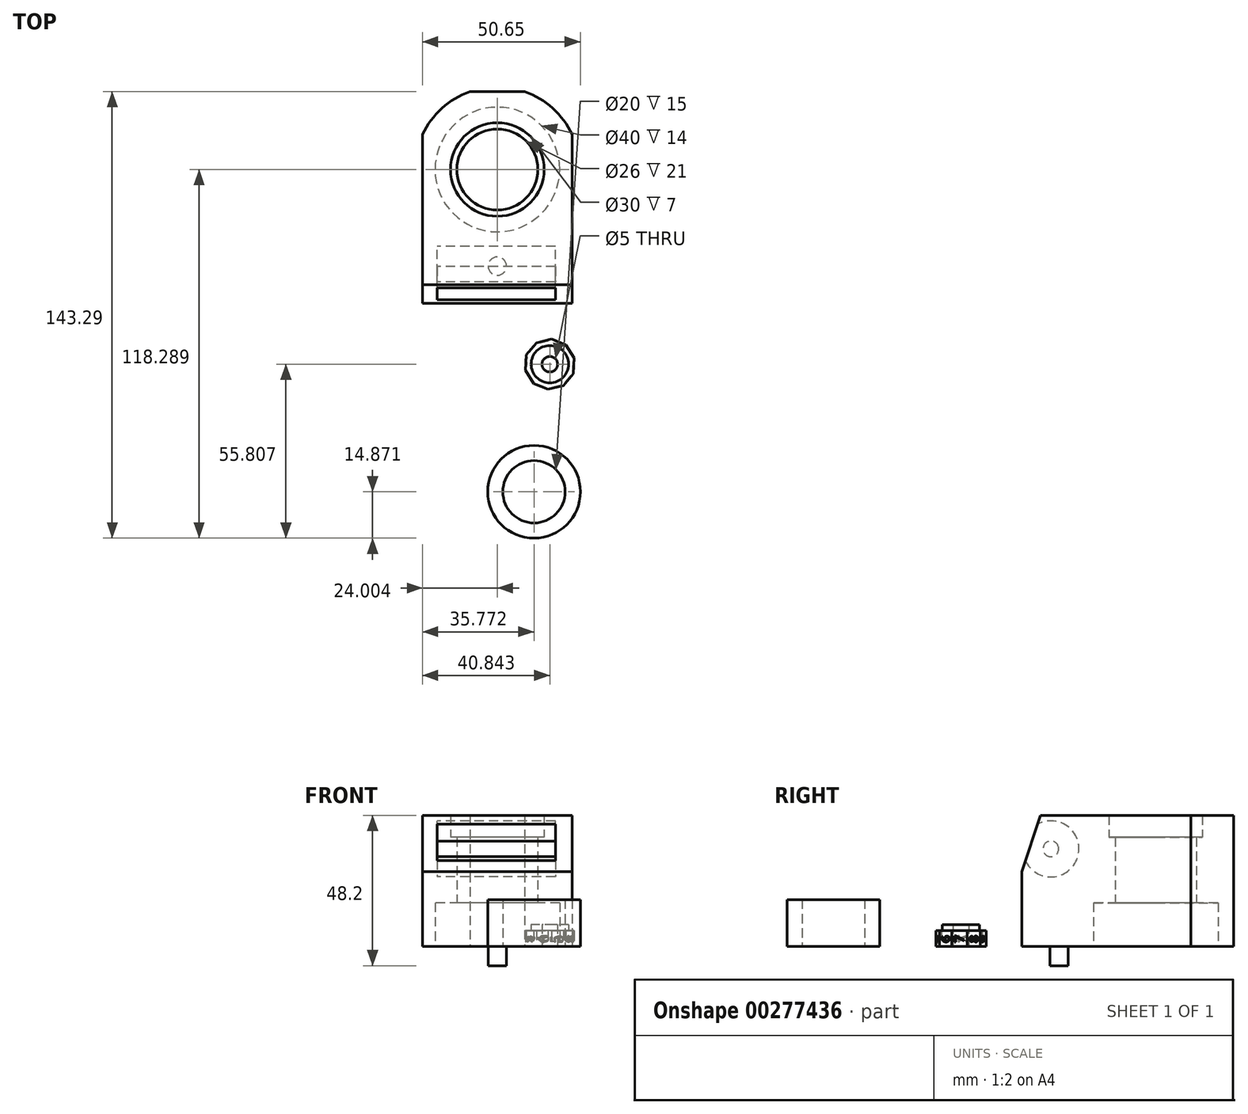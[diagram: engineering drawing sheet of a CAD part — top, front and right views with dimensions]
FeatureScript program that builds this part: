
annotation { "Feature Type Name" : "Feature", "Feature Type Description" : "" }
export const myFeature = defineFeature(function(context is Context, id is Id, definition is map)
    precondition{}
    {
        {
            var Q0;
            Q0=qCreatedBy(makeId("Top.planeOp"),FACE);
            var sketch = newSketch(context, id + "F0", { "sketchPlane" : qUnion([Q0])});
            skCircle(sketch, "E0.cCircle", {"center": v(-31.33, 0.84) * mm, "radius": 7.7 * mm, "construction": true});
            skLineSegment(sketch, "E0.0", {"start": v(-23.82, -2.17) * mm, "end": v(-27.02, -6) * mm});
            skLineSegment(sketch, "E0.1", {"start": v(-27.02, -6) * mm, "end": v(-31.86, -7.23) * mm});
            skLineSegment(sketch, "E0.2", {"start": v(-31.86, -7.23) * mm, "end": v(-36.5, -5.38) * mm});
            skLineSegment(sketch, "E0.3", {"start": v(-36.5, -5.38) * mm, "end": v(-39.17, -1.15) * mm});
            skLineSegment(sketch, "E0.4", {"start": v(-39.17, -1.15) * mm, "end": v(-38.84, 3.84) * mm});
            skLineSegment(sketch, "E0.5", {"start": v(-38.84, 3.84) * mm, "end": v(-35.64, 7.68) * mm});
            skLineSegment(sketch, "E0.6", {"start": v(-35.64, 7.68) * mm, "end": v(-30.8, 8.9) * mm});
            skLineSegment(sketch, "E0.7", {"start": v(-30.8, 8.9) * mm, "end": v(-26.15, 7.05) * mm});
            skLineSegment(sketch, "E0.8", {"start": v(-26.15, 7.05) * mm, "end": v(-23.48, 2.82) * mm});
            skLineSegment(sketch, "E0.9", {"start": v(-23.48, 2.82) * mm, "end": v(-23.82, -2.17) * mm});
            skPoint(sketch, "E0.0.midPoint", {"position": v(-25.42, -4.09) * mm});
            skCircle(sketch, "E1", {"center": v(-31.33, 0.84) * mm, "radius": 2.5 * mm});
            skSolve(sketch);
        }
        {
            var Q0;
            Q0=makeQuery(id+"F0.imprint","IMPRINT",FACE,{"disambiguationData":[TD([[makeQuery(id+"F0.imprint","IMPRINT",EDGE,{"derivedFrom":sQuery(id+"F0.wireOp",EDGE,"E0.0")}),-1.0]])]});
            extrude(context, id + "F1", {"entities" : qUnion([Q0]), "depth" : 5 * mm});
        }
        {
            var Q0;
            Q0=makeQuery(id+"F1.opExtrude","CAP_FACE",FACE,{"disambiguationData":[OSD([sQuery(id+"F0.wireOp",EDGE,"E0.0"),sQuery(id+"F0.wireOp",EDGE,"E0.1"),sQuery(id+"F0.wireOp",EDGE,"E0.2"),sQuery(id+"F0.wireOp",EDGE,"E0.3"),sQuery(id+"F0.wireOp",EDGE,"E0.4"),sQuery(id+"F0.wireOp",EDGE,"E0.5"),sQuery(id+"F0.wireOp",EDGE,"E0.6"),sQuery(id+"F0.wireOp",EDGE,"E0.7"),sQuery(id+"F0.wireOp",EDGE,"E0.8"),sQuery(id+"F0.wireOp",EDGE,"E0.9"),sQuery(id+"F0.wireOp",EDGE,"E1")])],"isStart":false});
            var sketch = newSketch(context, id + "F2", { "sketchPlane" : qUnion([Q0])});
            skCircle(sketch, "E2", {"center": v(-31.33, 0.84) * mm, "radius": 6 * mm});
            skSolve(sketch);
        }
        {
            var Q0;
            Q0=makeQuery(id+"F2.imprint","IMPRINT",FACE,{"disambiguationData":[TD([[makeQuery(id+"F2.imprint","IMPRINT",EDGE,{"derivedFrom":sQuery(id+"F2.wireOp",EDGE,"E2")}),1.0]])]});
            extrude(context, id + "F3", {"entities" : qUnion([Q0]), "operationType" : NewBodyOperationType.ADD, "depth" : 2 * mm});
        }
        {
            var Q0;
            Q0=makeQuery(id+"F1.opExtrude","SWEPT_FACE",FACE,{"disambiguationData":[OSD([sQuery(id+"F0.wireOp",EDGE,"E0.6")])]});
            var sketch = newSketch(context, id + "F4", { "sketchPlane" : qUnion([Q0])});
            skText(sketch, "E3", { "text": "0", "fontName": "OpenSans-Regular.ttf"});
            const initialGuessF4  = {"E3": [0.02861, 0.00365, 0, -1, 0.003]};
            skSetInitialGuess(sketch, initialGuessF4);
            skSolve(sketch);
        }
        {
            var Q0;
            Q0 = qSketchRegion(id + "F4", true);
            extrude(context, id + "F5", {"entities" : qUnion([Q0]), "operationType" : NewBodyOperationType.REMOVE, "oppositeDirection" : true, "depth" : 0.2 * mm});
        }
        {
            var Q0;
            Q0=makeQuery(id+"F1.opExtrude","SWEPT_FACE",FACE,{"disambiguationData":[OSD([sQuery(id+"F0.wireOp",EDGE,"E0.5")])]});
            var sketch = newSketch(context, id + "F6", { "sketchPlane" : qUnion([Q0])});
            skText(sketch, "E4", { "text": "1", "fontName": "OpenSans-Regular.ttf"});
            const initialGuessF6  = {"E4": [0.0208, 0.00138, 0, 1, 0.003]};
            skSetInitialGuess(sketch, initialGuessF6);
            skSolve(sketch);
        }
        {
            var Q0;
            Q0 = qSketchRegion(id + "F6", true);
            extrude(context, id + "F7", {"entities" : qUnion([Q0]), "operationType" : NewBodyOperationType.REMOVE, "oppositeDirection" : true, "depth" : 0.2 * mm});
        }
        {
            var Q0;
            Q0=makeQuery(id+"F1.opExtrude","SWEPT_FACE",FACE,{"disambiguationData":[OSD([sQuery(id+"F0.wireOp",EDGE,"E0.4")])]});
            var sketch = newSketch(context, id + "F8", { "sketchPlane" : qUnion([Q0])});
            skText(sketch, "E5", { "text": "2", "fontName": "OpenSans-Regular.ttf"});
            const initialGuessF8  = {"E5": [0.00264, 0.00125, 0, 1, 0.003]};
            skSetInitialGuess(sketch, initialGuessF8);
            skSolve(sketch);
        }
        {
            var Q0;
            Q0 = qSketchRegion(id + "F8", true);
            extrude(context, id + "F9", {"entities" : qUnion([Q0]), "operationType" : NewBodyOperationType.REMOVE, "oppositeDirection" : true, "depth" : 0.2 * mm});
        }
        {
            var Q0;
            Q0=makeQuery(id+"F1.opExtrude","SWEPT_FACE",FACE,{"disambiguationData":[OSD([sQuery(id+"F0.wireOp",EDGE,"E0.3")])]});
            var sketch = newSketch(context, id + "F10", { "sketchPlane" : qUnion([Q0])});
            skText(sketch, "E6", { "text": "3", "fontName": "OpenSans-Regular.ttf"});
            const initialGuessF10  = {"E6": [-0.01597, 0.00116, 0, 1, 0.003]};
            skSetInitialGuess(sketch, initialGuessF10);
            skSolve(sketch);
        }
        {
            var Q0;
            Q0 = qSketchRegion(id + "F10", true);
            extrude(context, id + "F11", {"entities" : qUnion([Q0]), "operationType" : NewBodyOperationType.REMOVE, "oppositeDirection" : true, "depth" : 0.2 * mm});
        }
        {
            var Q0;
            Q0=makeQuery(id+"F1.opExtrude","SWEPT_FACE",FACE,{"disambiguationData":[OSD([sQuery(id+"F0.wireOp",EDGE,"E0.2")])]});
            var sketch = newSketch(context, id + "F12", { "sketchPlane" : qUnion([Q0])});
            skText(sketch, "E7", { "text": "4", "fontName": "OpenSans-Regular.ttf"});
            const initialGuessF12  = {"E7": [-0.02786, 0.00106, 0, 1, 0.003]};
            skSetInitialGuess(sketch, initialGuessF12);
            skSolve(sketch);
        }
        {
            var Q0;
            Q0 = qSketchRegion(id + "F12", true);
            extrude(context, id + "F13", {"entities" : qUnion([Q0]), "operationType" : NewBodyOperationType.REMOVE, "oppositeDirection" : true, "depth" : 0.2 * mm});
        }
        {
            var Q0;
            Q0=makeQuery(id+"F1.opExtrude","SWEPT_FACE",FACE,{"disambiguationData":[OSD([sQuery(id+"F0.wireOp",EDGE,"E0.1")])]});
            var sketch = newSketch(context, id + "F14", { "sketchPlane" : qUnion([Q0])});
            skText(sketch, "E8", { "text": "5", "fontName": "OpenSans-Regular.ttf"});
            const initialGuessF14  = {"E8": [-0.0288, 0.00105, 0, 1, 0.003]};
            skSetInitialGuess(sketch, initialGuessF14);
            skSolve(sketch);
        }
        {
            var Q0;
            Q0 = qSketchRegion(id + "F14", true);
            extrude(context, id + "F15", {"entities" : qUnion([Q0]), "operationType" : NewBodyOperationType.REMOVE, "oppositeDirection" : true, "depth" : 0.2 * mm});
        }
        {
            var Q0;
            Q0=makeQuery(id+"F1.opExtrude","SWEPT_FACE",FACE,{"disambiguationData":[OSD([sQuery(id+"F0.wireOp",EDGE,"E0.0")])]});
            var sketch = newSketch(context, id + "F16", { "sketchPlane" : qUnion([Q0])});
            skText(sketch, "E9", { "text": "6", "fontName": "OpenSans-Regular.ttf"});
            const initialGuessF16  = {"E9": [-0.0179, 0.00116, 0, 1, 0.003]};
            skSetInitialGuess(sketch, initialGuessF16);
            skSolve(sketch);
        }
        {
            var Q0;
            Q0 = qSketchRegion(id + "F16", true);
            extrude(context, id + "F17", {"entities" : qUnion([Q0]), "operationType" : NewBodyOperationType.REMOVE, "oppositeDirection" : true, "depth" : 0.2 * mm});
        }
        {
            var Q0;
            Q0=makeQuery(id+"F1.opExtrude","SWEPT_FACE",FACE,{"disambiguationData":[OSD([sQuery(id+"F0.wireOp",EDGE,"E0.9")])]});
            var sketch = newSketch(context, id + "F18", { "sketchPlane" : qUnion([Q0])});
            skText(sketch, "E10", { "text": "7", "fontName": "OpenSans-Regular.ttf"});
            const initialGuessF18  = {"E10": [0.00025, 0.00121, 0, 1, 0.003]};
            skSetInitialGuess(sketch, initialGuessF18);
            skSolve(sketch);
        }
        {
            var Q0;
            Q0 = qSketchRegion(id + "F18", true);
            extrude(context, id + "F19", {"entities" : qUnion([Q0]), "operationType" : NewBodyOperationType.REMOVE, "oppositeDirection" : true, "depth" : 0.2 * mm});
        }
        {
            var Q0;
            Q0=makeQuery(id+"F1.opExtrude","SWEPT_FACE",FACE,{"disambiguationData":[OSD([sQuery(id+"F0.wireOp",EDGE,"E0.8")])]});
            var sketch = newSketch(context, id + "F20", { "sketchPlane" : qUnion([Q0])});
            skText(sketch, "E11", { "text": "8", "fontName": "OpenSans-Regular.ttf"});
            const initialGuessF20  = {"E11": [0.01895, 0.00118, 0, 1, 0.003]};
            skSetInitialGuess(sketch, initialGuessF20);
            skSolve(sketch);
        }
        {
            var Q0;
            Q0 = qSketchRegion(id + "F20", true);
            extrude(context, id + "F21", {"entities" : qUnion([Q0]), "operationType" : NewBodyOperationType.REMOVE, "oppositeDirection" : true, "depth" : 0.2 * mm});
        }
        {
            var Q0;
            Q0=makeQuery(id+"F1.opExtrude","SWEPT_FACE",FACE,{"disambiguationData":[OSD([sQuery(id+"F0.wireOp",EDGE,"E0.7")])]});
            var sketch = newSketch(context, id + "F22", { "sketchPlane" : qUnion([Q0])});
            skText(sketch, "E12", { "text": "9", "fontName": "OpenSans-Regular.ttf"});
            const initialGuessF22  = {"E12": [0.03078, 0.0011, 0, 1, 0.003]};
            skSetInitialGuess(sketch, initialGuessF22);
            skSolve(sketch);
        }
        {
            var Q0;
            Q0 = qSketchRegion(id + "F22", true);
            extrude(context, id + "F23", {"entities" : qUnion([Q0]), "operationType" : NewBodyOperationType.REMOVE, "oppositeDirection" : true, "depth" : 0.2 * mm});
        }
        {
            var Q0;
            Q0=qCreatedBy(makeId("Top.planeOp"),FACE);
            var sketch = newSketch(context, id + "F24", { "sketchPlane" : qUnion([Q0])});
            skLineSegment(sketch, "E13.bottom", {"start": v(-56.96, 88.32) * mm, "end": v(-39.38, 88.32) * mm});
            skLineSegment(sketch, "E13.top", {"start": v(-72.17, 20.32) * mm, "end": v(-24.17, 20.32) * mm});
            skLineSegment(sketch, "E13.left", {"start": v(-72.17, 74.55) * mm, "end": v(-72.17, 20.32) * mm});
            skLineSegment(sketch, "E13.right", {"start": v(-24.17, 74.55) * mm, "end": v(-24.17, 20.32) * mm});
            skArc(sketch, "E14", {"start": v(-56.96, 88.32) * mm, "mid": v(-65.95, 82.97) * mm, "end": v(-72.17, 74.55) * mm});
            skPoint(sketch, "E14.centerSnap0", {"position": v(-48.17, 88.32) * mm});
            skPoint(sketch, "E15.orphan", {"position": v(-72.17, 88.32) * mm});
            skArc(sketch, "E16.trimOffspring", {"start": v(-24.17, 74.55) * mm, "mid": v(-30.39, 82.97) * mm, "end": v(-39.38, 88.32) * mm});
            skPoint(sketch, "E17.orphan", {"position": v(-24.17, 88.32) * mm});
            skCircle(sketch, "E18", {"center": v(-48.17, 63.32) * mm, "radius": 20 * mm});
            skSolve(sketch);
        }
        {
            var Q0;
            Q0=makeQuery(id+"F24.imprint","IMPRINT",FACE,{"disambiguationData":[TD([[makeQuery(id+"F24.imprint","IMPRINT",EDGE,{"derivedFrom":sQuery(id+"F24.wireOp",EDGE,"E13.bottom")}),-1.0]])]});
            extrude(context, id + "F25", {"entities" : qUnion([Q0]), "depth" : 14 * mm});
        }
        {
            var Q0;
            Q0=makeQuery(id+"F25.opExtrude","CAP_FACE",FACE,{"disambiguationData":[OSD([sQuery(id+"F24.wireOp",EDGE,"E13.bottom"),sQuery(id+"F24.wireOp",EDGE,"E13.top"),sQuery(id+"F24.wireOp",EDGE,"E13.left"),sQuery(id+"F24.wireOp",EDGE,"E13.right"),sQuery(id+"F24.wireOp",EDGE,"E14"),sQuery(id+"F24.wireOp",EDGE,"E16.trimOffspring"),sQuery(id+"F24.wireOp",EDGE,"E18")])],"isStart":false});
            var sketch = newSketch(context, id + "F26", { "sketchPlane" : qUnion([Q0])});
            skLineSegment(sketch, "E19.0.0", {"start": v(-72.17, 74.55) * mm, "end": v(-72.17, 20.32) * mm});
            skLineSegment(sketch, "E19.0.1", {"start": v(-72.17, 20.32) * mm, "end": v(-24.17, 20.32) * mm});
            skLineSegment(sketch, "E19.0.2", {"start": v(-24.17, 20.32) * mm, "end": v(-24.17, 74.55) * mm});
            skArc(sketch, "E19.0.3", {"start": v(-24.17, 74.55) * mm, "mid": v(-30.39, 82.97) * mm, "end": v(-39.38, 88.32) * mm});
            skLineSegment(sketch, "E19.0.4", {"start": v(-39.38, 88.32) * mm, "end": v(-56.96, 88.32) * mm});
            skArc(sketch, "E19.0.5", {"start": v(-56.96, 88.32) * mm, "mid": v(-65.95, 82.97) * mm, "end": v(-72.17, 74.55) * mm});
            skCircle(sketch, "E20", {"center": v(-48.17, 63.32) * mm, "radius": 13 * mm});
            skSolve(sketch);
        }
        {
            var Q0;
            Q0=makeQuery(id+"F26.imprint","IMPRINT",FACE,{"disambiguationData":[TD([[makeQuery(id+"F26.imprint","IMPRINT",EDGE,{"derivedFrom":sQuery(id+"F26.wireOp",EDGE,"E19.0.0")}),1.0]])]});
            var Q1;
            Q1=makeQuery(id+"F26.imprint","IMPRINT",FACE,{"disambiguationData":[TD([[makeQuery(id+"F26.imprint","IMPRINT",EDGE,{"derivedFrom":sQuery(id+"F26.wireOp",EDGE,"E20")}),-1.0]])]});
            extrude(context, id + "F27", {"entities" : qUnion([Q0, Q1]), "operationType" : NewBodyOperationType.ADD, "depth" : 21 * mm});
        }
        {
            var Q0;
            Q0=makeQuery(id+"F27.opExtrude","CAP_FACE",FACE,{"disambiguationData":[OSD([sQuery(id+"F26.wireOp",EDGE,"E19.0.0"),sQuery(id+"F26.wireOp",EDGE,"E19.0.1"),sQuery(id+"F26.wireOp",EDGE,"E19.0.2"),sQuery(id+"F26.wireOp",EDGE,"E19.0.3"),sQuery(id+"F26.wireOp",EDGE,"E19.0.4"),sQuery(id+"F26.wireOp",EDGE,"E19.0.5"),sQuery(id+"F26.wireOp",EDGE,"E20")])],"isStart":false});
            var sketch = newSketch(context, id + "F28", { "sketchPlane" : qUnion([Q0])});
            skArc(sketch, "E21.0", {"start": v(-56.96, 88.32) * mm, "mid": v(-65.95, 82.97) * mm, "end": v(-72.17, 74.55) * mm});
            skLineSegment(sketch, "E22.0", {"start": v(-56.96, 88.32) * mm, "end": v(-39.38, 88.32) * mm});
            skArc(sketch, "E23.0", {"start": v(-24.17, 74.55) * mm, "mid": v(-30.39, 82.97) * mm, "end": v(-39.38, 88.32) * mm});
            skLineSegment(sketch, "E24.0", {"start": v(-24.17, 74.55) * mm, "end": v(-24.17, 20.32) * mm});
            skLineSegment(sketch, "E25.0.1", {"start": v(-72.17, 74.55) * mm, "end": v(-72.17, 20.32) * mm});
            skLineSegment(sketch, "E25.0.2", {"start": v(-72.17, 20.32) * mm, "end": v(-24.17, 20.32) * mm});
            skLineSegment(sketch, "E25.0.3", {"start": v(-24.17, 20.32) * mm, "end": v(-24.17, 74.55) * mm});
            skLineSegment(sketch, "E25.0.5", {"start": v(-39.38, 88.32) * mm, "end": v(-56.96, 88.32) * mm});
            skCircle(sketch, "E26", {"center": v(-48.17, 63.32) * mm, "radius": 15 * mm});
            skSolve(sketch);
        }
        {
            var Q0;
            Q0=makeQuery(id+"F28.imprint","IMPRINT",FACE,{"disambiguationData":[TD([[makeQuery(id+"F28.imprint","IMPRINT",EDGE,{"derivedFrom":sQuery(id+"F28.wireOp",EDGE,"E21.0")}),1.0]])]});
            extrude(context, id + "F29", {"entities" : qUnion([Q0]), "operationType" : NewBodyOperationType.ADD, "depth" : 7 * mm});
        }
        {
            var Q0;
            Q0=makeQuery(id+"F25.opExtrude","CAP_FACE",FACE,{"disambiguationData":[OSD([sQuery(id+"F24.wireOp",EDGE,"E13.bottom"),sQuery(id+"F24.wireOp",EDGE,"E13.top"),sQuery(id+"F24.wireOp",EDGE,"E13.left"),sQuery(id+"F24.wireOp",EDGE,"E13.right"),sQuery(id+"F24.wireOp",EDGE,"E14"),sQuery(id+"F24.wireOp",EDGE,"E16.trimOffspring"),sQuery(id+"F24.wireOp",EDGE,"E18")])],"isStart":true});
            var sketch = newSketch(context, id + "F30", { "sketchPlane" : qUnion([Q0])});
            skCircle(sketch, "E27", {"center": v(-48.17, -32.32) * mm, "radius": 2.95 * mm});
            skPoint(sketch, "E27.centerSnap0", {"position": v(-48.17, -20.32) * mm});
            skSolve(sketch);
        }
        {
            var Q0;
            Q0=makeQuery(id+"F30.imprint","IMPRINT",FACE,{"disambiguationData":[TD([[makeQuery(id+"F30.imprint","IMPRINT",EDGE,{"derivedFrom":sQuery(id+"F30.wireOp",EDGE,"E27")}),1.0]])]});
            extrude(context, id + "F31", {"entities" : qUnion([Q0]), "operationType" : NewBodyOperationType.ADD, "depth" : 6.2 * mm});
        }
        {
            var Q0;
            Q0=makeQuery(id+"F29.boolean.opBoolean","MERGE",FACE,{"derivedFrom":[makeQuery(id+"F27.boolean.opBoolean","MERGE",FACE,{"derivedFrom":[makeQuery(id+"F25.opExtrude","SWEPT_FACE",FACE,{"disambiguationData":[OSD([sQuery(id+"F24.wireOp",EDGE,"E13.right")])]}),makeQuery(id+"F27.opExtrude","SWEPT_FACE",FACE,{"disambiguationData":[OSD([sQuery(id+"F26.wireOp",EDGE,"E19.0.2")])]})]}),makeQuery(id+"F29.opExtrude","SWEPT_FACE",FACE,{"disambiguationData":[OSD([sQuery(id+"F28.wireOp",EDGE,"E25.0.3")])]})]});
            var sketch = newSketch(context, id + "F32", { "sketchPlane" : qUnion([Q0])});
            skLineSegment(sketch, "E28", {"start": v(20.32, 42) * mm, "end": v(26.32, 42) * mm});
            skLineSegment(sketch, "E29", {"start": v(20.32, 42) * mm, "end": v(20.32, 24) * mm});
            skLineSegment(sketch, "E30", {"start": v(20.32, 24) * mm, "end": v(26.32, 42) * mm});
            skSolve(sketch);
        }
        {
            var Q0;
            Q0=makeQuery(id+"F32.imprint","IMPRINT",FACE,{"disambiguationData":[TD([[makeQuery(id+"F32.imprint","IMPRINT",EDGE,{"derivedFrom":sQuery(id+"F32.wireOp",EDGE,"E28")}),1.0]])]});
            extrude(context, id + "F33", {"entities" : qUnion([Q0]), "operationType" : NewBodyOperationType.REMOVE, "endBound" : BoundingType.UP_TO_NEXT, "oppositeDirection" : true, "depth" : 25 * mm});
        }
        {
            var Q0;
            Q0=qCreatedBy(makeId("Top.planeOp"),FACE);
            var sketch = newSketch(context, id + "F34", { "sketchPlane" : qUnion([Q0])});
            skCircle(sketch, "E31", {"center": v(-36.4, -40.1) * mm, "radius": 14.88 * mm});
            skCircle(sketch, "E32", {"center": v(-36.4, -40.1) * mm, "radius": 10 * mm});
            skSolve(sketch);
        }
        {
            var Q0;
            Q0=makeQuery(id+"F34.imprint","IMPRINT",FACE,{"disambiguationData":[TD([[makeQuery(id+"F34.imprint","IMPRINT",EDGE,{"derivedFrom":sQuery(id+"F34.wireOp",EDGE,"E31")}),1.0]])]});
            extrude(context, id + "F35", {"entities" : qUnion([Q0]), "depth" : 15 * mm});
        }
        {
            var Q0;
            Q0=qCreatedBy(makeId("Right.planeOp"),FACE);
            var sketch = newSketch(context, id + "F36", { "sketchPlane" : qUnion([Q0])});
            skCircle(sketch, "E33", {"center": v(42.3, 66.29) * mm, "radius": 9 * mm});
            skCircle(sketch, "E34", {"center": v(42.3, 66.29) * mm, "radius": 2.5 * mm});
            skSolve(sketch);
        }
        {
            var Q0;
            Q0=makeQuery(id+"F36.imprint","IMPRINT",FACE,{"disambiguationData":[TD([[makeQuery(id+"F36.imprint","IMPRINT",EDGE,{"derivedFrom":sQuery(id+"F36.wireOp",EDGE,"E33")}),1.0]])]});
            extrude(context, id + "F37", {"entities" : qUnion([Q0]), "depth" : 38 * mm});
        }
        {
            var Q0;
            Q0=makeQuery(id+"F37.opExtrude","SWEPT_BODY",BODY,{"disambiguationData":[OSD([sQuery(id+"F36.wireOp",EDGE,"E33"),sQuery(id+"F36.wireOp",EDGE,"E34")])]});
            transform(context, id + "F38", {"entities" : qUnion([Q0]), "transformType" : TransformType.TRANSLATION_3D, "dx" : -67.5 * mm, "dy" : -12.6 * mm, "dz" : -35 * mm, "makeCopy" : false});
        }
        {
            var Q0;
            Q0=makeQuery(id+"F37.opExtrude","SWEPT_BODY",BODY,{"disambiguationData":[OSD([sQuery(id+"F36.wireOp",EDGE,"E33"),sQuery(id+"F36.wireOp",EDGE,"E34")])]});
            var Q1;
            Q1=makeQuery(id+"F25.opExtrude","SWEPT_BODY",BODY,{"disambiguationData":[OSD([sQuery(id+"F24.wireOp",EDGE,"E13.bottom"),sQuery(id+"F24.wireOp",EDGE,"E13.top"),sQuery(id+"F24.wireOp",EDGE,"E13.left"),sQuery(id+"F24.wireOp",EDGE,"E13.right"),sQuery(id+"F24.wireOp",EDGE,"E14"),sQuery(id+"F24.wireOp",EDGE,"E16.trimOffspring"),sQuery(id+"F24.wireOp",EDGE,"E18")])]});
            booleanBodies(context, id + "F39", {"operationType" : BooleanOperationType.SUBTRACTION, "tools" : qUnion([Q0]), "targets" : qUnion([Q1])});
        }
    });
